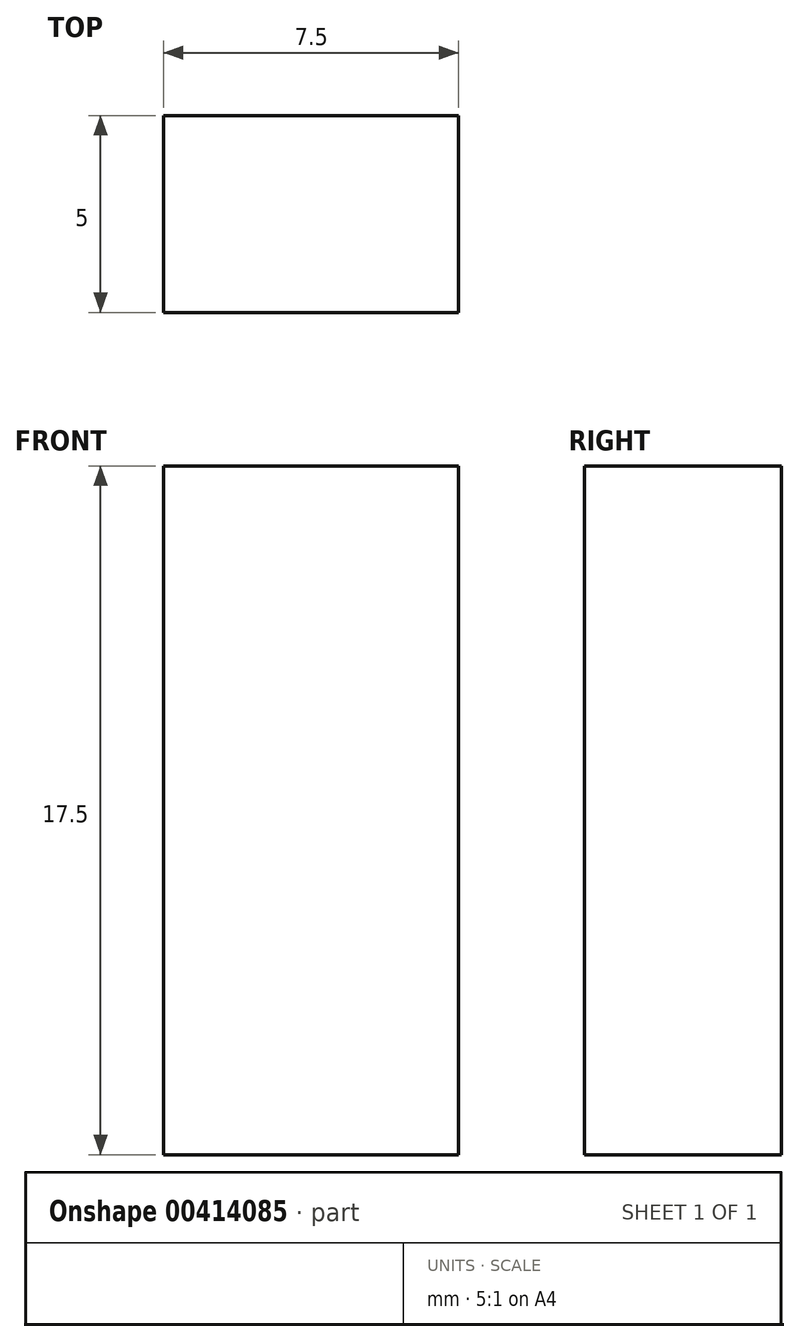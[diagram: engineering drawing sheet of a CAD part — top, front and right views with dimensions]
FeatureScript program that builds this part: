
annotation { "Feature Type Name" : "Feature", "Feature Type Description" : "" }
export const myFeature = defineFeature(function(context is Context, id is Id, definition is map)
    precondition{}
    {
        {
            var Q0;
            Q0=qCreatedBy(makeId("Front.planeOp"),FACE);
            var sketch = newSketch(context, id + "F0", { "sketchPlane" : qUnion([Q0])});
            skLineSegment(sketch, "E0.bottom", {"start": v(0, 0) * mm, "end": v(7.5, 0) * mm});
            skLineSegment(sketch, "E0.top", {"start": v(0, 17.5) * mm, "end": v(7.5, 17.5) * mm});
            skLineSegment(sketch, "E0.left", {"start": v(0, 0) * mm, "end": v(0, 17.5) * mm});
            skLineSegment(sketch, "E0.right", {"start": v(7.5, 0) * mm, "end": v(7.5, 17.5) * mm});
            skSolve(sketch);
        }
        {
            var Q0;
            Q0=makeQuery(id+"F0.imprint","IMPRINT",FACE,{"disambiguationData":[TD([[makeQuery(id+"F0.imprint","IMPRINT",EDGE,{"derivedFrom":sQuery(id+"F0.wireOp",EDGE,"E0.bottom")}),1.0]])]});
            extrude(context, id + "F1", {"entities" : qUnion([Q0]), "depth" : 5 * mm});
        }
    });
